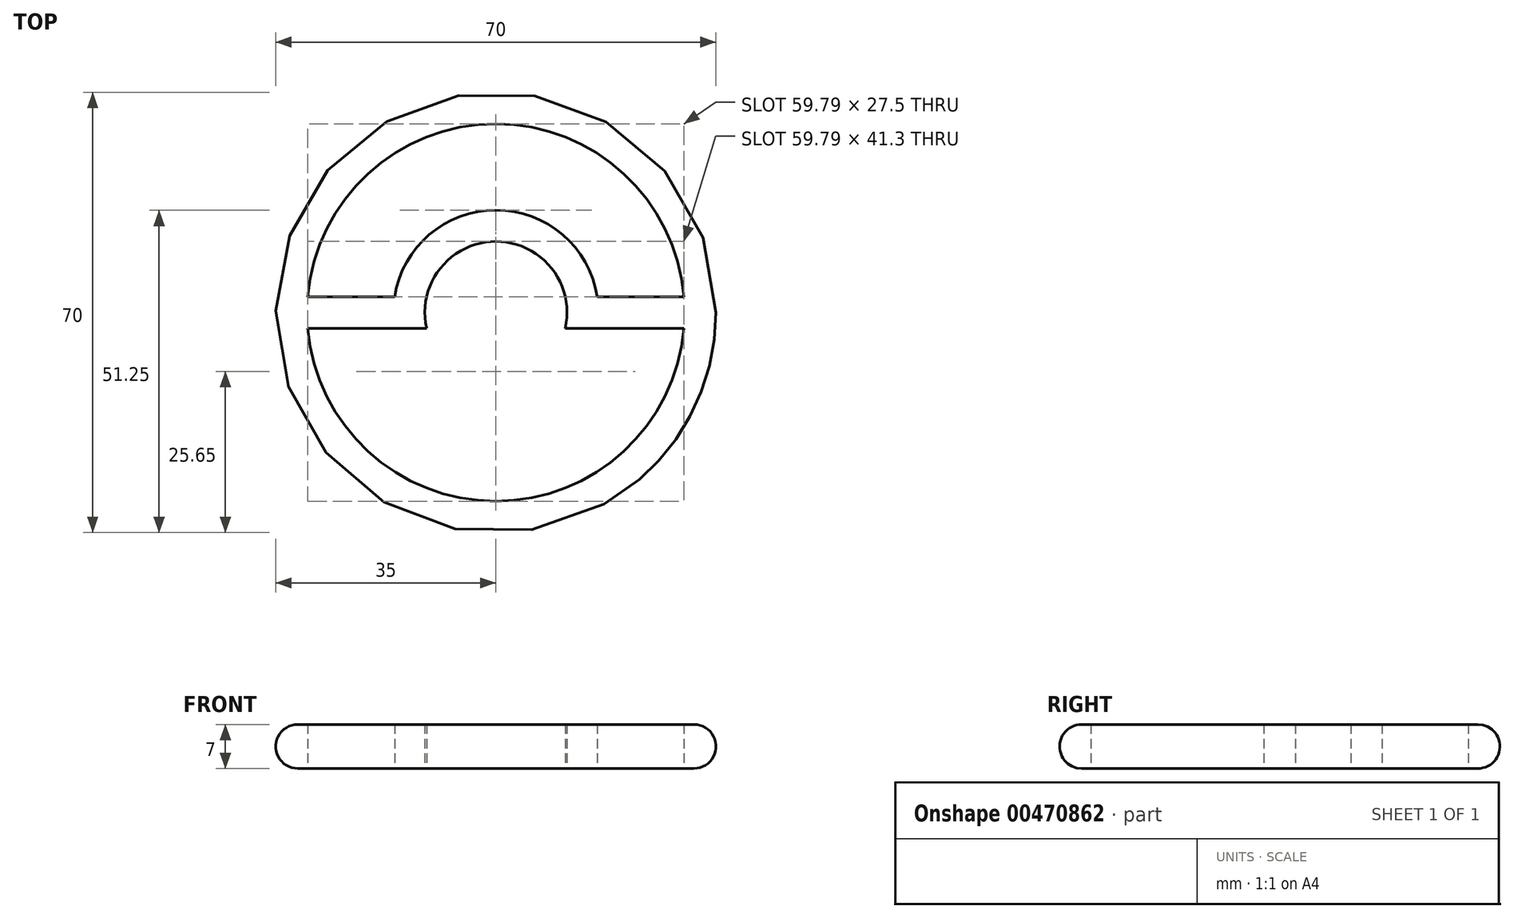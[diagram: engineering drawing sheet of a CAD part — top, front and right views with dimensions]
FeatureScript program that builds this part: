
annotation { "Feature Type Name" : "Feature", "Feature Type Description" : "" }
export const myFeature = defineFeature(function(context is Context, id is Id, definition is map)
    precondition{}
    {
        {
            var Q0;
            Q0=qCreatedBy(makeId("Top.planeOp"),FACE);
            var sketch = newSketch(context, id + "F0", { "sketchPlane" : qUnion([Q0])});
            skCircle(sketch, "E0", {"center": v(0, 0) * mm, "radius": 11.3 * mm});
            skCircle(sketch, "E1", {"center": v(0, 0) * mm, "radius": 35 * mm});
            skCircle(sketch, "E2", {"center": v(0, 0) * mm, "radius": 16.3 * mm});
            skLineSegment(sketch, "E3", {"start": v(-34.91, 2.5) * mm, "end": v(34.91, 2.5) * mm});
            skLineSegment(sketch, "E4", {"start": v(34.91, -2.5) * mm, "end": v(-34.91, -2.5) * mm});
            skCircle(sketch, "E5", {"center": v(0, 0) * mm, "radius": 30 * mm});
            skSolve(sketch);
        }
        {
            var Q0;
            Q0 = qSketchRegion(id + "F0", true);
            var Q1;
            {var subQ0=sQuery(id+"F0.wireOp",EDGE,"E3");var subQ1=sQuery(id+"F0.wireOp",EDGE,"E2");var subQ2=makeQuery(id+"F0.imprint","INTERSECT",VERTEX,{"disambiguationData":[OD(0.0)],"derivedFrom":[subQ1,subQ0]});Q1=makeQuery(id+"F0.imprint","IMPRINT",FACE,{"disambiguationData":[TD([[makeQuery(id+"F0.imprint","IMPRINT",EDGE,{"disambiguationData":[TD([[subQ2,-1.0]])],"derivedFrom":subQ1}),-1.0]])]});}
            var Q2;
            {var subQ0=sQuery(id+"F0.wireOp",EDGE,"E3");var subQ1=sQuery(id+"F0.wireOp",EDGE,"E0");var subQ2=makeQuery(id+"F0.imprint","INTERSECT",VERTEX,{"disambiguationData":[OD(0.0)],"derivedFrom":[subQ1,subQ0]});Q2=makeQuery(id+"F0.imprint","IMPRINT",FACE,{"disambiguationData":[TD([[makeQuery(id+"F0.imprint","IMPRINT",EDGE,{"disambiguationData":[TD([[subQ2,-1.0]])],"derivedFrom":subQ1}),-1.0]])]});}
            var Q3;
            {var subQ0=sQuery(id+"F0.wireOp",EDGE,"E3");var subQ1=sQuery(id+"F0.wireOp",EDGE,"E0");var subQ2=makeQuery(id+"F0.imprint","INTERSECT",VERTEX,{"disambiguationData":[OD(0.0)],"derivedFrom":[subQ1,subQ0]});Q3=makeQuery(id+"F0.imprint","IMPRINT",FACE,{"disambiguationData":[TD([[makeQuery(id+"F0.imprint","IMPRINT",EDGE,{"disambiguationData":[TD([[subQ2,1.0]])],"derivedFrom":subQ1}),-1.0]])]});}
            var Q4;
            {var subQ0=sQuery(id+"F0.wireOp",EDGE,"E4");var subQ1=sQuery(id+"F0.wireOp",EDGE,"E0");var subQ2=makeQuery(id+"F0.imprint","INTERSECT",VERTEX,{"disambiguationData":[OD(0.0)],"derivedFrom":[subQ1,subQ0]});Q4=makeQuery(id+"F0.imprint","IMPRINT",FACE,{"disambiguationData":[TD([[makeQuery(id+"F0.imprint","IMPRINT",EDGE,{"disambiguationData":[TD([[subQ2,-1.0]])],"derivedFrom":subQ1}),-1.0]])]});}
            var Q5;
            {var subQ0=sQuery(id+"F0.wireOp",EDGE,"E3");var subQ1=sQuery(id+"F0.wireOp",EDGE,"E2");var subQ2=makeQuery(id+"F0.imprint","INTERSECT",VERTEX,{"disambiguationData":[OD(1.0)],"derivedFrom":[subQ1,subQ0]});Q5=makeQuery(id+"F0.imprint","IMPRINT",FACE,{"disambiguationData":[TD([[makeQuery(id+"F0.imprint","IMPRINT",EDGE,{"disambiguationData":[TD([[subQ2,1.0]])],"derivedFrom":subQ1}),-1.0]])]});}
            var Q6;
            {var subQ0=sQuery(id+"F0.wireOp",EDGE,"E3");var subQ1=sQuery(id+"F0.wireOp",EDGE,"E0");var subQ2=makeQuery(id+"F0.imprint","INTERSECT",VERTEX,{"disambiguationData":[OD(1.0)],"derivedFrom":[subQ1,subQ0]});Q6=makeQuery(id+"F0.imprint","IMPRINT",FACE,{"disambiguationData":[TD([[makeQuery(id+"F0.imprint","IMPRINT",EDGE,{"disambiguationData":[TD([[subQ2,1.0]])],"derivedFrom":subQ1}),-1.0]])]});}
            extrude(context, id + "F1", {"entities" : qUnion([Q0, Q1, Q2, Q3, Q4, Q5, Q6]), "depth" : 7 * mm});
        }
        {
            var Q0;
            Q0=makeQuery(id+"F1.opExtrude","CAP_EDGE",EDGE,{"disambiguationData":[OSD([sQuery(id+"F0.wireOp",EDGE,"E1")])],"isStart":false});
            fillet(context, id + "F2", {"entities" : qUnion([Q0]), "radius" : 3.5 * mm, "tangentPropagation" : true, "allowEdgeOverflow" : false});
        }
        {
            var Q0;
            Q0=makeQuery(id+"F1.opExtrude","CAP_EDGE",EDGE,{"disambiguationData":[OSD([sQuery(id+"F0.wireOp",EDGE,"E1")])],"isStart":true});
            fillet(context, id + "F3", {"entities" : qUnion([Q0]), "radius" : 3.5 * mm, "tangentPropagation" : true, "allowEdgeOverflow" : false});
        }
    });
